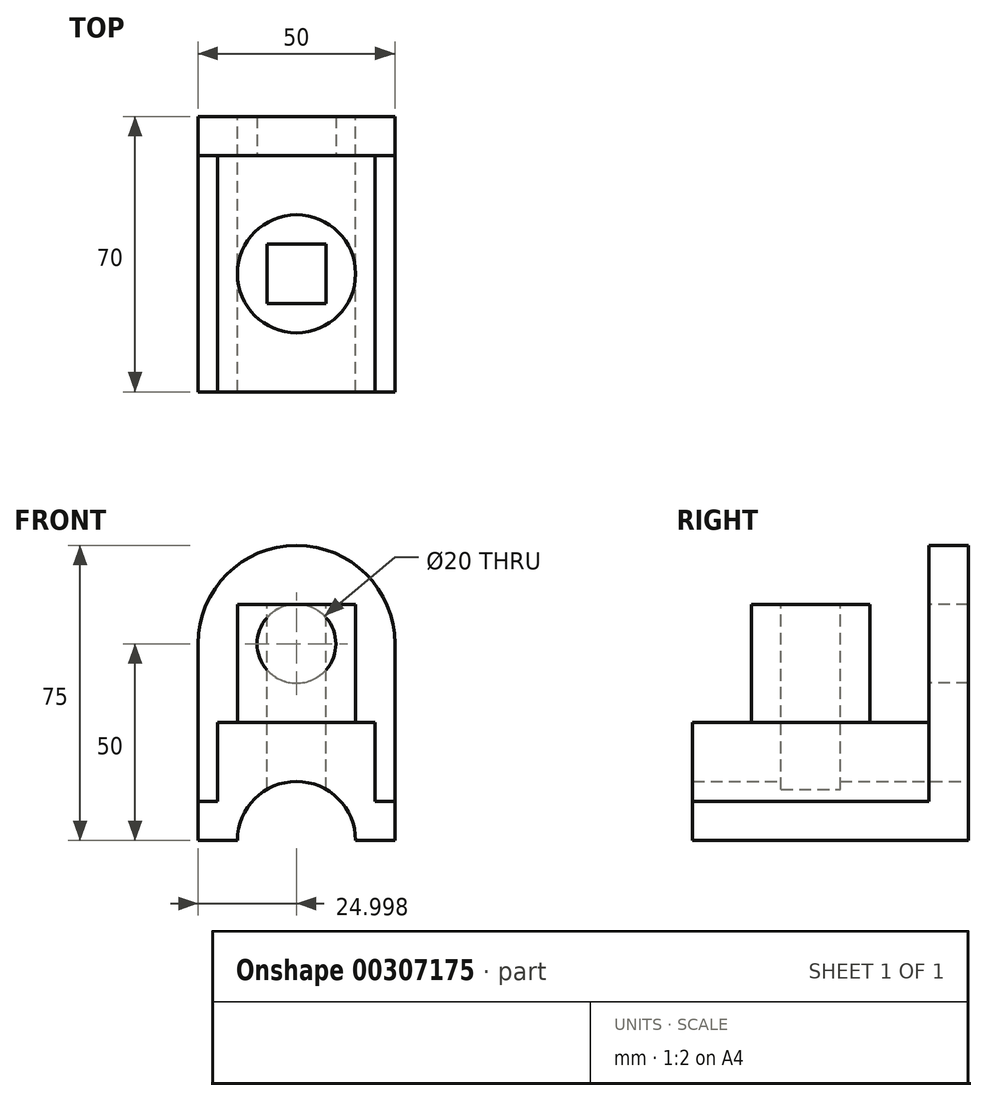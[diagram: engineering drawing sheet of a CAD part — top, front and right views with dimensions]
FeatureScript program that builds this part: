
annotation { "Feature Type Name" : "Feature", "Feature Type Description" : "" }
export const myFeature = defineFeature(function(context is Context, id is Id, definition is map)
    precondition{}
    {
        {
            var Q0;
            Q0=qCreatedBy(makeId("Front.planeOp"),FACE);
            var sketch = newSketch(context, id + "F0", { "sketchPlane" : qUnion([Q0])});
            skLineSegment(sketch, "E0.bottom", {"start": v(15.89, 0) * mm, "end": v(-24.11, 0) * mm});
            skLineSegment(sketch, "E0.top", {"start": v(15.89, 30) * mm, "end": v(-24.11, 30) * mm});
            skLineSegment(sketch, "E0.left", {"start": v(15.89, 0) * mm, "end": v(15.89, 30) * mm});
            skLineSegment(sketch, "E0.right", {"start": v(-24.11, 0) * mm, "end": v(-24.11, 30) * mm});
            skLineSegment(sketch, "E1", {"start": v(-24.11, 0) * mm, "end": v(-29.11, 0) * mm});
            skLineSegment(sketch, "E2", {"start": v(-29.11, 0) * mm, "end": v(-29.11, 10) * mm});
            skLineSegment(sketch, "E3", {"start": v(-29.11, 10) * mm, "end": v(-24.11, 10) * mm});
            skLineSegment(sketch, "E4.bottom", {"start": v(15.89, 0) * mm, "end": v(20.89, 0) * mm});
            skLineSegment(sketch, "E4.top", {"start": v(15.89, 10) * mm, "end": v(20.89, 10) * mm});
            skLineSegment(sketch, "E4.left", {"start": v(15.89, 0) * mm, "end": v(15.89, 10) * mm});
            skLineSegment(sketch, "E4.right", {"start": v(20.89, 0) * mm, "end": v(20.89, 10) * mm});
            skCircle(sketch, "E5", {"center": v(-4.11, 0) * mm, "radius": 15 * mm});
            skSolve(sketch);
        }
        {
            var Q0;
            {var subQ0=sQuery(id+"F0.wireOp",EDGE,"E1");Q0=makeQuery(id+"F0.imprint","IMPRINT",FACE,{"disambiguationData":[TD([[makeQuery(id+"F0.imprint","IMPRINT",EDGE,{"derivedFrom":subQ0}),-1.0]])]});}
            var Q1;
            Q1=makeQuery(id+"F0.imprint","IMPRINT",FACE,{"disambiguationData":[TD([[makeQuery(id+"F0.imprint","IMPRINT",EDGE,{"derivedFrom":sQuery(id+"F0.wireOp",EDGE,"E4.bottom")}),1.0]])]});
            var Q2;
            {var subQ0=sQuery(id+"F0.wireOp",EDGE,"E0.top");Q2=makeQuery(id+"F0.imprint","IMPRINT",FACE,{"disambiguationData":[TD([[makeQuery(id+"F0.imprint","IMPRINT",EDGE,{"derivedFrom":subQ0}),1.0]])]});}
            extrude(context, id + "F1", {"entities" : qUnion([Q0, Q1, Q2]), "depth" : 60 * mm});
        }
        {
            var Q0;
            Q0=makeQuery(id+"F1.opExtrude","CAP_FACE",FACE,{"disambiguationData":[OSD([sQuery(id+"F0.wireOp",EDGE,"E0.bottom"),sQuery(id+"F0.wireOp",EDGE,"E0.top"),sQuery(id+"F0.wireOp",EDGE,"E0.left"),sQuery(id+"F0.wireOp",EDGE,"E0.right"),sQuery(id+"F0.wireOp",EDGE,"E1"),sQuery(id+"F0.wireOp",EDGE,"E2"),sQuery(id+"F0.wireOp",EDGE,"E3"),sQuery(id+"F0.wireOp",EDGE,"E4.bottom"),sQuery(id+"F0.wireOp",EDGE,"E4.top"),sQuery(id+"F0.wireOp",EDGE,"E4.right"),sQuery(id+"F0.wireOp",EDGE,"E5")])],"isStart":true});
            var sketch = newSketch(context, id + "F2", { "sketchPlane" : qUnion([Q0])});
            skLineSegment(sketch, "E6.bottom", {"start": v(-20.89, 0) * mm, "end": v(29.11, 0) * mm});
            skLineSegment(sketch, "E6.top", {"start": v(-20.89, 50) * mm, "end": v(29.11, 50) * mm});
            skLineSegment(sketch, "E6.left", {"start": v(-20.89, 0) * mm, "end": v(-20.89, 50) * mm});
            skLineSegment(sketch, "E6.right", {"start": v(29.11, 0) * mm, "end": v(29.11, 50) * mm});
            skCircle(sketch, "E7", {"center": v(4.11, 50) * mm, "radius": 10 * mm});
            skCircle(sketch, "E8", {"center": v(4.11, 50) * mm, "radius": 25 * mm});
            skSolve(sketch);
        }
        {
            var Q0;
            {var subQ6=makeQuery(id+"F1.opExtrude","CAP_EDGE",EDGE,{"disambiguationData":[OSD([sQuery(id+"F0.wireOp",EDGE,"E0.left")])],"isStart":true});Q0=makeQuery(id+"F2.imprint","IMPRINT",FACE,{"disambiguationData":[TD([[makeQuery(id+"F2.imprint","IMPRINT",EDGE,{"derivedFrom":subQ6}),1.0]])]});}
            var Q1;
            {var subQ2=makeQuery(id+"F1.opExtrude","CAP_EDGE",EDGE,{"disambiguationData":[OSD([sQuery(id+"F0.wireOp",EDGE,"E0.left")])],"isStart":true});Q1=makeQuery(id+"F2.imprint","IMPRINT",FACE,{"disambiguationData":[TD([[makeQuery(id+"F2.imprint","IMPRINT",EDGE,{"derivedFrom":subQ2}),-1.0]])]});}
            var Q2;
            {var subQ0=makeQuery(id+"F1.opExtrude","CAP_EDGE",EDGE,{"disambiguationData":[OSD([sQuery(id+"F0.wireOp",EDGE,"E0.right")])],"isStart":true});Q2=makeQuery(id+"F2.imprint","IMPRINT",FACE,{"disambiguationData":[TD([[makeQuery(id+"F2.imprint","IMPRINT",EDGE,{"derivedFrom":subQ0}),-1.0]])]});}
            var Q3;
            {var subQ0=sQuery(id+"F2.wireOp",EDGE,"E8");var subQ1=makeQuery(id+"F1.opExtrude","CAP_EDGE",EDGE,{"disambiguationData":[OSD([sQuery(id+"F0.wireOp",EDGE,"E0.top")])],"isStart":true});var subQ2=makeQuery(id+"F2.imprint","INTERSECT",VERTEX,{"disambiguationData":[OD(0.0)],"derivedFrom":[subQ1,subQ0]});Q3=makeQuery(id+"F2.imprint","IMPRINT",FACE,{"disambiguationData":[TD([[makeQuery(id+"F2.imprint","IMPRINT",EDGE,{"disambiguationData":[TD([[subQ2,-1.0]])],"derivedFrom":subQ0}),1.0]])]});}
            var Q4;
            {var subQ0=sQuery(id+"F2.wireOp",EDGE,"E7");var subQ1=sQuery(id+"F2.wireOp",EDGE,"E6.top");var subQ2=makeQuery(id+"F2.imprint","INTERSECT",VERTEX,{"disambiguationData":[OD(0.0)],"derivedFrom":[subQ1,subQ0]});Q4=makeQuery(id+"F2.imprint","IMPRINT",FACE,{"disambiguationData":[TD([[makeQuery(id+"F2.imprint","IMPRINT",EDGE,{"disambiguationData":[TD([[subQ2,-1.0]])],"derivedFrom":subQ0}),-1.0]])]});}
            var Q5;
            {var subQ1=sQuery(id+"F2.wireOp",EDGE,"E6.top");var subQ3=sQuery(id+"F2.wireOp",EDGE,"E7");var subQ4=makeQuery(id+"F2.imprint","INTERSECT",VERTEX,{"disambiguationData":[OD(0.0)],"derivedFrom":[subQ1,subQ3]});Q5=makeQuery(id+"F2.imprint","IMPRINT",FACE,{"disambiguationData":[TD([[makeQuery(id+"F2.imprint","IMPRINT",EDGE,{"disambiguationData":[TD([[subQ4,1.0]])],"derivedFrom":subQ3}),-1.0]])]});}
            extrude(context, id + "F3", {"entities" : qUnion([Q0, Q1, Q2, Q3, Q4, Q5]), "operationType" : NewBodyOperationType.ADD, "depth" : 10 * mm});
        }
        {
            var Q0;
            Q0=makeQuery(id+"F1.opExtrude","SWEPT_FACE",FACE,{"disambiguationData":[OSD([sQuery(id+"F0.wireOp",EDGE,"E0.top")])]});
            var sketch = newSketch(context, id + "F4", { "sketchPlane" : qUnion([Q0])});
            skCircle(sketch, "E9", {"center": v(-4.11, -30) * mm, "radius": 15 * mm});
            skPoint(sketch, "E9.centerSnap0", {"position": v(15.89, -30) * mm});
            skPoint(sketch, "E9.centerSnap1", {"position": v(-4.11, 0) * mm});
            skSolve(sketch);
        }
        {
            var Q0;
            Q0=makeQuery(id+"F4.imprint","IMPRINT",FACE,{"disambiguationData":[TD([[makeQuery(id+"F4.imprint","IMPRINT",EDGE,{"derivedFrom":sQuery(id+"F4.wireOp",EDGE,"E9")}),1.0]])]});
            extrude(context, id + "F5", {"entities" : qUnion([Q0]), "operationType" : NewBodyOperationType.ADD, "depth" : 30 * mm});
        }
        {
            var Q0;
            Q0=makeQuery(id+"F5.opExtrude","CAP_FACE",FACE,{"disambiguationData":[OSD([sQuery(id+"F4.wireOp",EDGE,"E9")])],"isStart":false});
            var sketch = newSketch(context, id + "F6", { "sketchPlane" : qUnion([Q0])});
            skLineSegment(sketch, "E10.bottom", {"start": v(3.39, -37.5) * mm, "end": v(-11.61, -37.5) * mm});
            skLineSegment(sketch, "E10.top", {"start": v(3.39, -22.5) * mm, "end": v(-11.61, -22.5) * mm});
            skLineSegment(sketch, "E10.left", {"start": v(3.39, -37.5) * mm, "end": v(3.39, -22.5) * mm});
            skLineSegment(sketch, "E10.right", {"start": v(-11.61, -37.5) * mm, "end": v(-11.61, -22.5) * mm});
            skPoint(sketch, "E10.middle", {"position": v(-4.11, -30) * mm});
            skSolve(sketch);
        }
        {
            var Q0;
            Q0=makeQuery(id+"F6.imprint","IMPRINT",FACE,{"disambiguationData":[TD([[makeQuery(id+"F6.imprint","IMPRINT",EDGE,{"derivedFrom":sQuery(id+"F6.wireOp",EDGE,"E10.bottom")}),-1.0]])]});
            extrude(context, id + "F7", {"entities" : qUnion([Q0]), "operationType" : NewBodyOperationType.REMOVE, "oppositeDirection" : true, "depth" : 70 * mm});
        }
    });
